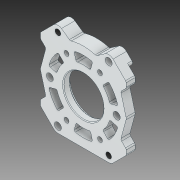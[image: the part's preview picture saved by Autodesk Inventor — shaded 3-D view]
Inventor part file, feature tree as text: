
AUTODESK INVENTOR PART (.ipt)
format: ipt  version: 2019 (Build 230136000, 136)  size: 240,640 bytes
history: native  units: in
note: dims shown in document units (in); Inventor stores cm internally (conversion verified against a paired STEP export)
features: chamfer x1
ambient origin geometry x8: Origin, YZ Plane, XZ Plane, XY Plane, X Axis, Y Axis, Z Axis, Center Point
bodies: Solid1 (feature_tree)
feature tree (1):
  chamfer  "Chamfer1"  [1 undecoded]
note: 1 required parameter value undecoded (feature->parameter linkage not recoverable at this tier; creation-order binding heuristic only, values carry confidence <= 0.55)
